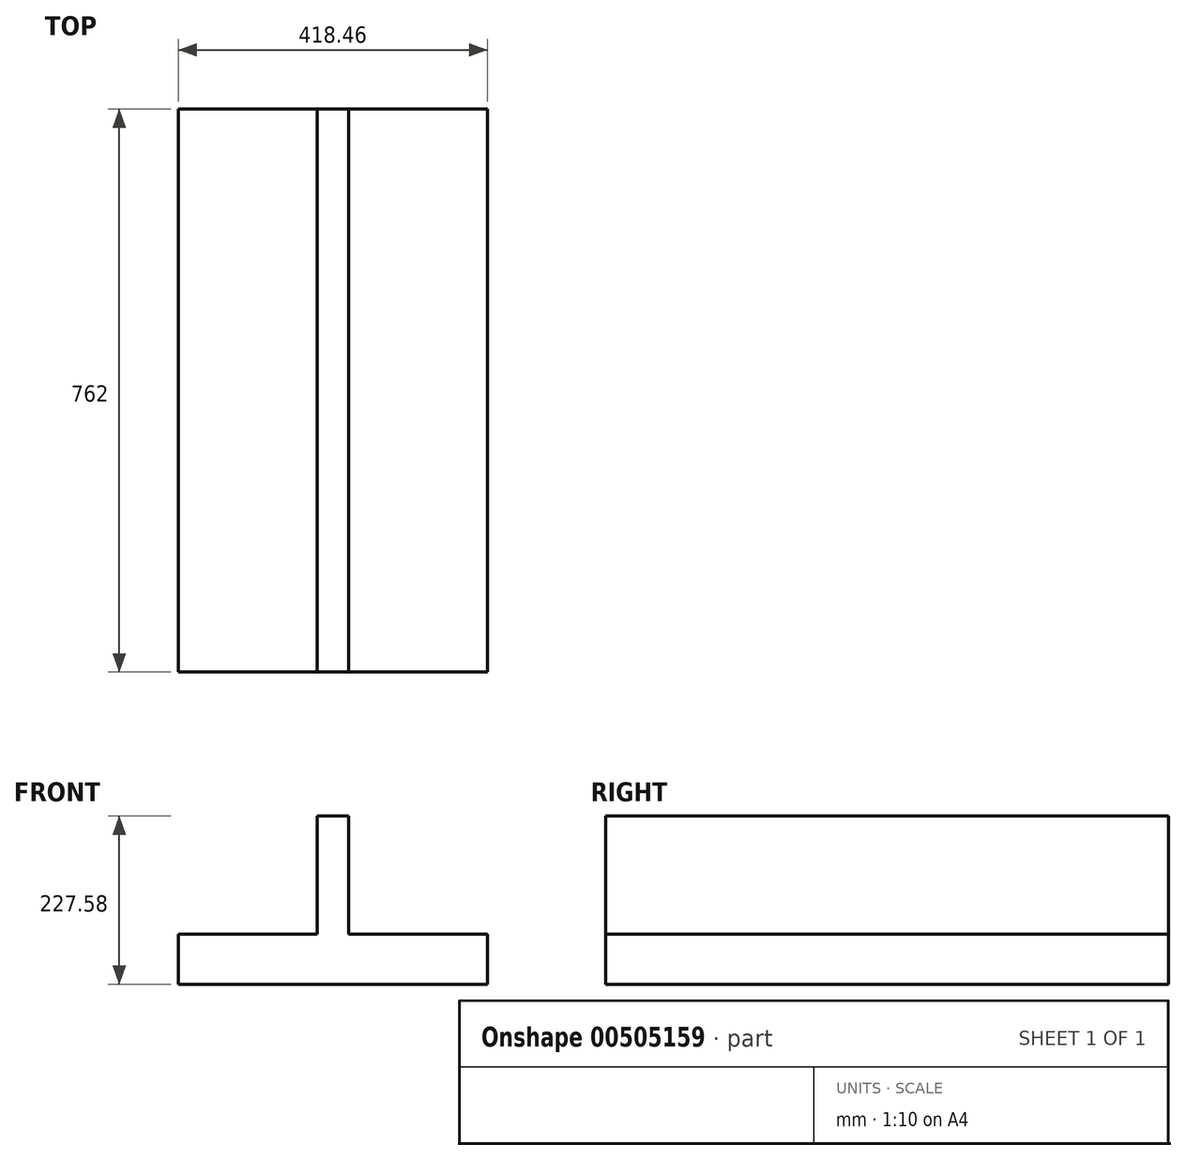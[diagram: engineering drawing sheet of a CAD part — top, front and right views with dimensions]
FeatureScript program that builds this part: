
annotation { "Feature Type Name" : "Feature", "Feature Type Description" : "" }
export const myFeature = defineFeature(function(context is Context, id is Id, definition is map)
    precondition{}
    {
        {
            var Q0;
            Q0=qCreatedBy(makeId("Front.planeOp"),FACE);
            var sketch = newSketch(context, id + "F0", { "sketchPlane" : qUnion([Q0])});
            skLineSegment(sketch, "E0.bottom", {"start": v(209.23, 33.78) * mm, "end": v(-209.23, 33.78) * mm});
            skLineSegment(sketch, "E0.top", {"start": v(209.23, -33.78) * mm, "end": v(-209.23, -33.78) * mm});
            skLineSegment(sketch, "E0.left", {"start": v(209.23, 33.78) * mm, "end": v(209.23, -33.78) * mm});
            skLineSegment(sketch, "E0.right", {"start": v(-209.23, 33.78) * mm, "end": v(-209.23, -33.78) * mm});
            skPoint(sketch, "E0.middle", {"position": v(0, 0) * mm});
            skLineSegment(sketch, "E1", {"start": v(0, 0) * mm, "end": v(0, 193.8) * mm});
            skLineSegment(sketch, "E2", {"start": v(0, -33.78) * mm, "end": v(21.02, -33.78) * mm});
            skLineSegment(sketch, "E3", {"start": v(0, -33.78) * mm, "end": v(-21.02, -33.78) * mm});
            skLineSegment(sketch, "E4", {"start": v(0, -33.78) * mm, "end": v(0, 0) * mm});
            skLineSegment(sketch, "E5", {"start": v(21.02, -33.78) * mm, "end": v(21.02, 193.8) * mm});
            skLineSegment(sketch, "E6", {"start": v(21.02, 193.8) * mm, "end": v(0, 193.8) * mm});
            skLineSegment(sketch, "E7", {"start": v(-21.02, 193.8) * mm, "end": v(0, 193.8) * mm});
            skLineSegment(sketch, "E8", {"start": v(-21.02, -33.78) * mm, "end": v(-21.02, 193.8) * mm});
            skSolve(sketch);
        }
        {
            var Q0;
            Q0 = qSketchRegion(id + "F0", true);
            extrude(context, id + "F1", {"entities" : qUnion([Q0]), "depth" : 762 * mm});
        }
    });
